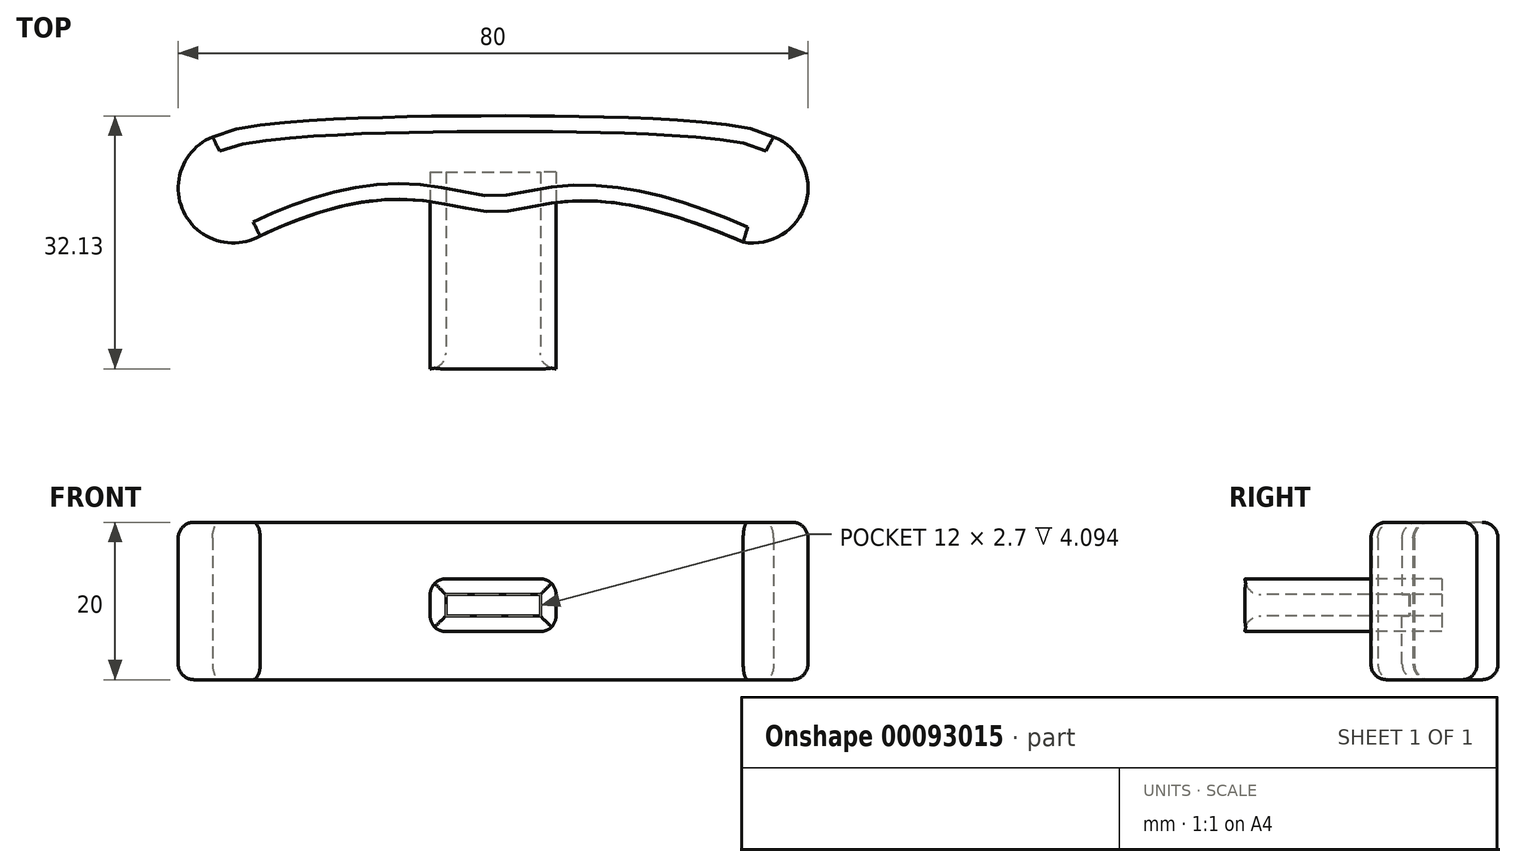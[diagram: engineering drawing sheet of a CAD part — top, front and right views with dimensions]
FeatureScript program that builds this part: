
annotation { "Feature Type Name" : "Feature", "Feature Type Description" : "" }
export const myFeature = defineFeature(function(context is Context, id is Id, definition is map)
    precondition{}
    {
        {
            var Q0;
            Q0=qCreatedBy(makeId("Top.planeOp"),FACE);
            var sketch = newSketch(context, id + "F0", { "sketchPlane" : qUnion([Q0])});
            skArc(sketch, "E0", {"start": v(-35.63, 4.46) * mm, "mid": v(-39.3, -5.06) * mm, "end": v(-29.58, -8.13) * mm});
            skFitSpline(sketch, "E1", {"points": [v(-35.63, 4.46) * mm, v(0, 7.13) * mm, v(35.63, 4.46) * mm], "startDerivative": vector(21.25, 12.57) * mm, "endDerivative": vector(18.8, -13.43) * mm});
            skFitSpline(sketch, "E2.MirrorCS", {"points": [v(-29.58, -8.13) * mm, v(0, -5.05) * mm, v(31.77, -8.92) * mm], "startDerivative": vector(104.39, 49.7) * mm, "endDerivative": vector(119.98, -52.53) * mm});
            skLineSegment(sketch, "E3", {"start": v(0, 9.31) * mm, "end": v(0, -13.75) * mm, "construction": true});
            skArc(sketch, "E4.MirrorC", {"start": v(35.63, 4.46) * mm, "mid": v(39.73, -3.97) * mm, "end": v(31.77, -8.92) * mm});
            skSolve(sketch);
        }
        {
            var Q0;
            Q0=makeQuery(id+"F0.imprint","IMPRINT",FACE,{"disambiguationData":[TD([[makeQuery(id+"F0.imprint","IMPRINT",EDGE,{"derivedFrom":sQuery(id+"F0.wireOp",EDGE,"E0")}),1.0]])]});
            extrude(context, id + "F1", {"entities" : qUnion([Q0]), "depth" : 20 * mm});
        }
        {
            var Q0;
            Q0=qCreatedBy(makeId("Front.planeOp"),FACE);
            var sketch = newSketch(context, id + "F2", { "sketchPlane" : qUnion([Q0])});
            skLineSegment(sketch, "E5.bottom", {"start": v(6, 8.11) * mm, "end": v(-6, 8.11) * mm});
            skLineSegment(sketch, "E5.top", {"start": v(6, 10.81) * mm, "end": v(-6, 10.81) * mm});
            skLineSegment(sketch, "E5.left", {"start": v(6, 8.11) * mm, "end": v(6, 10.81) * mm});
            skLineSegment(sketch, "E5.right", {"start": v(-6, 8.11) * mm, "end": v(-6, 10.81) * mm});
            skPoint(sketch, "E5.middle", {"position": v(0, 9.46) * mm});
            skSolve(sketch);
        }
        {
            var Q0;
            Q0=makeQuery(id+"F2.imprint","IMPRINT",FACE,{"disambiguationData":[TD([[makeQuery(id+"F2.imprint","IMPRINT",EDGE,{"derivedFrom":sQuery(id+"F2.wireOp",EDGE,"E5.bottom")}),-1.0]])]});
            extrude(context, id + "F3", {"entities" : qUnion([Q0]), "depth" : 25 * mm});
        }
        {
            var Q0;
            Q0=makeQuery(id+"F3.opExtrude","CAP_FACE",FACE,{"disambiguationData":[OSD([sQuery(id+"F2.wireOp",EDGE,"E5.bottom"),sQuery(id+"F2.wireOp",EDGE,"E5.top"),sQuery(id+"F2.wireOp",EDGE,"E5.left"),sQuery(id+"F2.wireOp",EDGE,"E5.right")])],"isStart":false});
            var sketch = newSketch(context, id + "F4", { "sketchPlane" : qUnion([Q0])});
            skLineSegment(sketch, "E6.0", {"start": v(-8, 6.11) * mm, "end": v(8, 6.11) * mm});
            skLineSegment(sketch, "E6.1", {"start": v(-8, 12.81) * mm, "end": v(-8, 6.11) * mm});
            skLineSegment(sketch, "E6.2", {"start": v(8, 12.81) * mm, "end": v(-8, 12.81) * mm});
            skLineSegment(sketch, "E6.3", {"start": v(8, 6.11) * mm, "end": v(8, 12.81) * mm});
            skSolve(sketch);
        }
        {
            var Q0;
            Q0=makeQuery(id+"F4.imprint","IMPRINT",FACE,{"disambiguationData":[TD([[makeQuery(id+"F4.imprint","IMPRINT",EDGE,{"derivedFrom":sQuery(id+"F4.wireOp",EDGE,"E6.0")}),1.0]])]});
            extrude(context, id + "F5", {"entities" : qUnion([Q0]), "oppositeDirection" : true, "depth" : 25 * mm});
        }
        {
            var Q0;
            Q0=makeQuery(id+"F3.opExtrude","CAP_FACE",FACE,{"disambiguationData":[OSD([sQuery(id+"F2.wireOp",EDGE,"E5.bottom"),sQuery(id+"F2.wireOp",EDGE,"E5.top"),sQuery(id+"F2.wireOp",EDGE,"E5.left"),sQuery(id+"F2.wireOp",EDGE,"E5.right")])],"isStart":false});
            extrude(context, id + "F6", {"entities" : qUnion([Q0]), "operationType" : NewBodyOperationType.REMOVE, "oppositeDirection" : true, "depth" : 25 * mm});
        }
        {
            var Q0;
            Q0=makeQuery(id+"F5.opExtrude","SWEPT_EDGE",EDGE,{"disambiguationData":[OSD([sQuery(id+"F4.wireOp",EDGE,"E6.2"),sQuery(id+"F4.wireOp",EDGE,"E6.3")])]});
            var Q1;
            Q1=makeQuery(id+"F5.opExtrude","SWEPT_EDGE",EDGE,{"disambiguationData":[OSD([sQuery(id+"F4.wireOp",EDGE,"E6.1"),sQuery(id+"F4.wireOp",EDGE,"E6.2")])]});
            var Q2;
            Q2=makeQuery(id+"F5.opExtrude","SWEPT_EDGE",EDGE,{"disambiguationData":[OSD([sQuery(id+"F4.wireOp",EDGE,"E6.0"),sQuery(id+"F4.wireOp",EDGE,"E6.3")])]});
            var Q3;
            Q3=makeQuery(id+"F5.opExtrude","SWEPT_EDGE",EDGE,{"disambiguationData":[OSD([sQuery(id+"F4.wireOp",EDGE,"E6.0"),sQuery(id+"F4.wireOp",EDGE,"E6.1")])]});
            fillet(context, id + "F7", {"entities" : qUnion([Q0, Q1, Q2, Q3]), "radius" : 2 * mm, "tangentPropagation" : true, "allowEdgeOverflow" : false});
        }
        {
            var Q0;
            Q0=makeQuery(id+"F1.opExtrude","CAP_EDGE",EDGE,{"disambiguationData":[OSD([sQuery(id+"F0.wireOp",EDGE,"E2.MirrorCS")])],"isStart":false});
            var Q1;
            Q1=makeQuery(id+"F1.opExtrude","CAP_EDGE",EDGE,{"disambiguationData":[OSD([sQuery(id+"F0.wireOp",EDGE,"E4.MirrorC")])],"isStart":false});
            var Q2;
            Q2=makeQuery(id+"F1.opExtrude","CAP_EDGE",EDGE,{"disambiguationData":[OSD([sQuery(id+"F0.wireOp",EDGE,"E0")])],"isStart":false});
            var Q3;
            Q3=makeQuery(id+"F1.opExtrude","CAP_EDGE",EDGE,{"disambiguationData":[OSD([sQuery(id+"F0.wireOp",EDGE,"E1")])],"isStart":false});
            var Q4;
            Q4=makeQuery(id+"F1.opExtrude","CAP_EDGE",EDGE,{"disambiguationData":[OSD([sQuery(id+"F0.wireOp",EDGE,"E2.MirrorCS")])],"isStart":true});
            var Q5;
            Q5=makeQuery(id+"F1.opExtrude","CAP_EDGE",EDGE,{"disambiguationData":[OSD([sQuery(id+"F0.wireOp",EDGE,"E4.MirrorC")])],"isStart":true});
            var Q6;
            Q6=makeQuery(id+"F1.opExtrude","CAP_EDGE",EDGE,{"disambiguationData":[OSD([sQuery(id+"F0.wireOp",EDGE,"E1")])],"isStart":true});
            var Q7;
            Q7=makeQuery(id+"F1.opExtrude","CAP_EDGE",EDGE,{"disambiguationData":[OSD([sQuery(id+"F0.wireOp",EDGE,"E0")])],"isStart":true});
            fillet(context, id + "F8", {"entities" : qUnion([Q0, Q1, Q2, Q3, Q4, Q5, Q6, Q7]), "radius" : 2 * mm, "tangentPropagation" : true, "allowEdgeOverflow" : false});
        }
        {
            var Q0;
            Q0=makeQuery(id+"F5.opExtrude","CAP_EDGE",EDGE,{"disambiguationData":[OSD([sQuery(id+"F2.wireOp",EDGE,"E5.top")])],"isStart":true});
            var Q1;
            Q1=makeQuery(id+"F5.opExtrude","CAP_EDGE",EDGE,{"disambiguationData":[OSD([sQuery(id+"F2.wireOp",EDGE,"E5.left")])],"isStart":true});
            var Q2;
            Q2=makeQuery(id+"F5.opExtrude","CAP_EDGE",EDGE,{"disambiguationData":[OSD([sQuery(id+"F2.wireOp",EDGE,"E5.bottom")])],"isStart":true});
            var Q3;
            Q3=makeQuery(id+"F5.opExtrude","CAP_EDGE",EDGE,{"disambiguationData":[OSD([sQuery(id+"F2.wireOp",EDGE,"E5.right")])],"isStart":true});
            fillet(context, id + "F9", {"entities" : qUnion([Q0, Q1, Q2, Q3]), "radius" : 2 * mm, "tangentPropagation" : true, "allowEdgeOverflow" : false});
        }
    });
